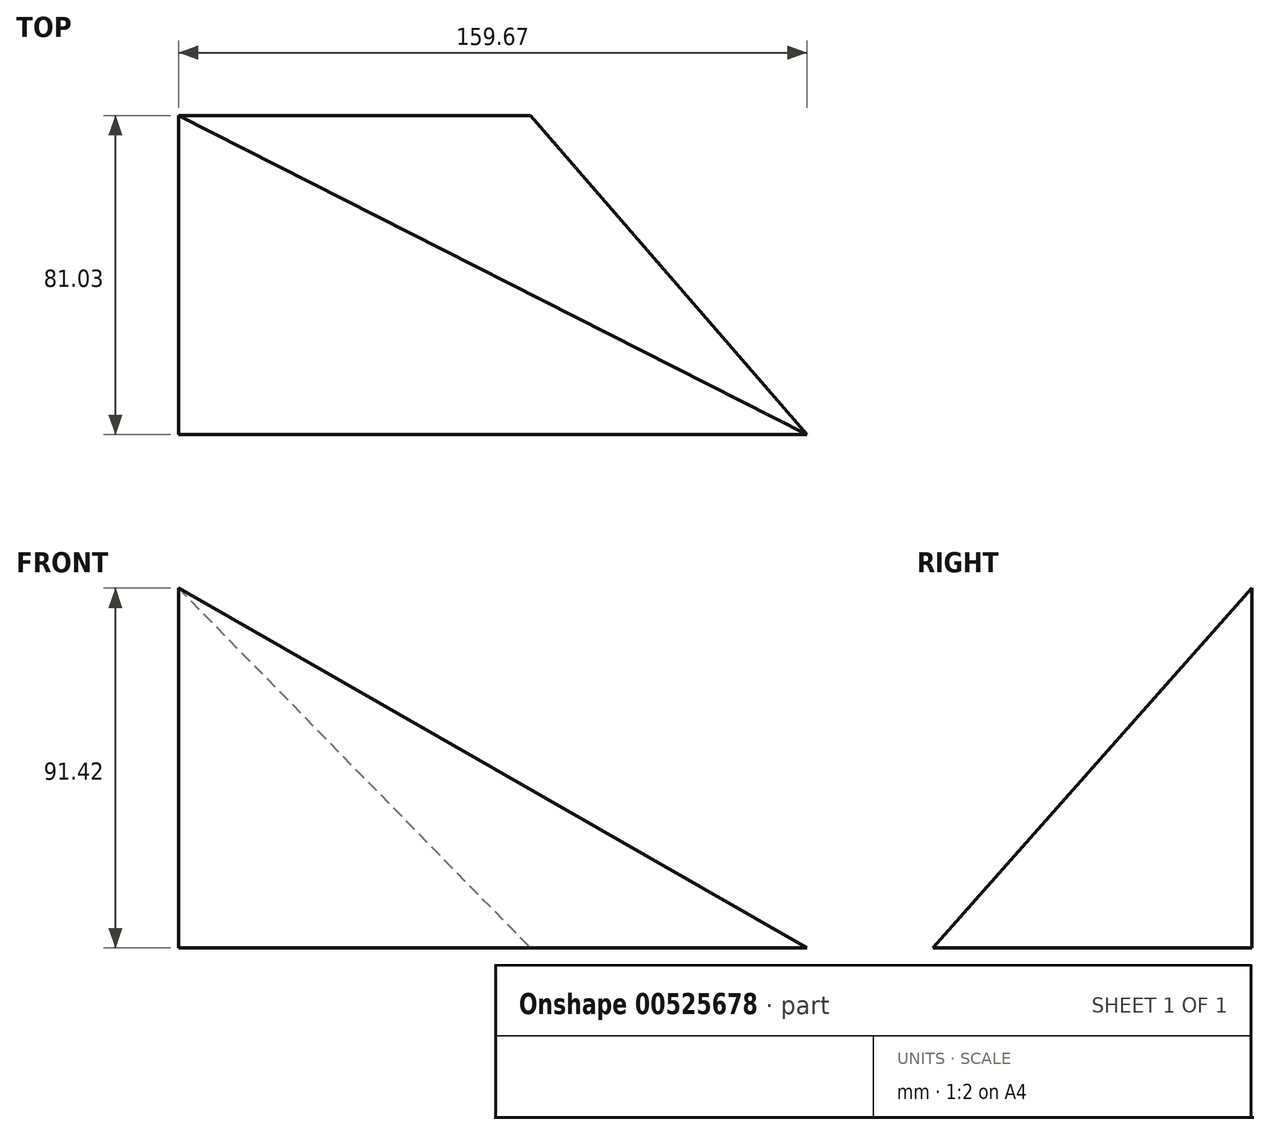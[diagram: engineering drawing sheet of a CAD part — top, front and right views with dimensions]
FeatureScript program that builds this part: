
annotation { "Feature Type Name" : "Feature", "Feature Type Description" : "" }
export const myFeature = defineFeature(function(context is Context, id is Id, definition is map)
    precondition{}
    {
        {
            var Q0;
            Q0=qCreatedBy(makeId("Front.planeOp"),FACE);
            var sketch = newSketch(context, id + "F0", { "sketchPlane" : qUnion([Q0])});
            skLineSegment(sketch, "E0.bottom", {"start": v(-85.6, 40.23) * mm, "end": v(74.08, 40.23) * mm});
            skLineSegment(sketch, "E0.top", {"start": v(-85.6, -51.19) * mm, "end": v(74.08, -51.19) * mm});
            skLineSegment(sketch, "E0.left", {"start": v(-85.6, 40.23) * mm, "end": v(-85.6, -51.19) * mm});
            skLineSegment(sketch, "E0.right", {"start": v(74.08, 40.23) * mm, "end": v(74.08, -51.19) * mm});
            skSolve(sketch);
        }
        {
            var Q0;
            Q0 = qSketchRegion(id + "F0", true);
            extrude(context, id + "F1", {"entities" : qUnion([Q0]), "depth" : 81.03 * mm, "offsetDistance" : 25.4 * mm});
        }
        {
            var Q0;
            Q0=makeQuery(id+"F1.opExtrude","SWEPT_FACE",FACE,{"disambiguationData":[OSD([sQuery(id+"F0.wireOp",EDGE,"E0.right")])]});
            var sketch = newSketch(context, id + "F2", { "sketchPlane" : qUnion([Q0])});
            skLineSegment(sketch, "E1", {"start": v(0, 40.23) * mm, "end": v(-81.03, -51.19) * mm});
            skLineSegment(sketch, "E2", {"start": v(-81.03, -51.19) * mm, "end": v(0, -51.19) * mm});
            skLineSegment(sketch, "E3", {"start": v(0, -51.19) * mm, "end": v(0, 40.23) * mm});
            skSolve(sketch);
        }
        {
            var Q0;
            Q0=makeQuery(id+"F2.imprint","IMPRINT",FACE,{"disambiguationData":[TD([[makeQuery(id+"F2.imprint","IMPRINT",EDGE,{"derivedFrom":sQuery(id+"F2.wireOp",EDGE,"E1")}),-1.0]])]});
            extrude(context, id + "F3", {"entities" : qUnion([Q0]), "operationType" : NewBodyOperationType.REMOVE, "endBound" : BoundingType.THROUGH_ALL, "oppositeDirection" : true, "depth" : 172.97 * mm, "offsetDistance" : 25.4 * mm});
        }
        {
            var Q0;
            Q0=makeQuery(id+"F3.boolean.opBoolean","COPY",FACE,{"derivedFrom":makeQuery(id+"F3.opExtrude","SWEPT_FACE",FACE,{"disambiguationData":[OSD([sQuery(id+"F2.wireOp",EDGE,"E1")])]})});
            var sketch = newSketch(context, id + "F4", { "sketchPlane" : qUnion([Q0])});
            skLineSegment(sketch, "E4", {"start": v(-85.6, 30.1) * mm, "end": v(74.08, -92.05) * mm});
            skLineSegment(sketch, "E5", {"start": v(74.08, -92.05) * mm, "end": v(-85.6, -92.05) * mm});
            skLineSegment(sketch, "E6", {"start": v(-85.6, -92.05) * mm, "end": v(-85.6, 30.1) * mm});
            skSolve(sketch);
        }
        {
            var Q0;
            Q0=makeQuery(id+"F4.imprint","IMPRINT",FACE,{"disambiguationData":[TD([[makeQuery(id+"F4.imprint","IMPRINT",EDGE,{"derivedFrom":sQuery(id+"F4.wireOp",EDGE,"E4")}),1.0]])]});
            extrude(context, id + "F5", {"entities" : qUnion([Q0]), "operationType" : NewBodyOperationType.REMOVE, "endBound" : BoundingType.THROUGH_ALL, "oppositeDirection" : true, "depth" : 25.4 * mm, "offsetDistance" : 25.4 * mm});
        }
    });
